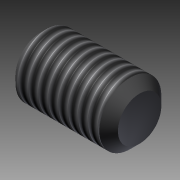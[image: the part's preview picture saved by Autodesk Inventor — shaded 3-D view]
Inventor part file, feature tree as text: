
AUTODESK INVENTOR PART (.ipt)
format: ipt  version: 2011 SP1 (Build 150282100, 282)  size: 117,248 bytes
history: native  units: mm
features: other x7, sketch x3, revolve x2, thread x1, extrude x1
ambient origin geometry x8: Origin, YZ Plane, XZ Plane, XY Plane, X Axis, Y Axis, Z Axis, Center Point
bodies: Solid1 (feature_tree)
feature tree (14):
  revolve  "Revolution1"  [1 undecoded]
  thread  "Thread1"  [1 undecoded]
  extrude  "Extrusion1"  TaperAngle=0.0deg  [1 undecoded]
  revolve  "Revolution2"  [1 undecoded]
  other  "CP_XY"
  other  "CP_YZ"
  other  "CP_ZX"
  other  "CP_X"
  other  "CP_Y"
  other  "CP_Z"
  other  "CP_Center"
  sketch  "Sketch_1"  dims[d0=360.0deg d1=6.7595mm d2=0.0mm d3=2.0mm d4=0.0mm]
  sketch  "Sketch_2"  dims[d5=360.0deg d6=0.0mm]
  sketch  "Sketch_3"
note: 4 required parameter values undecoded (feature->parameter linkage not recoverable at this tier; creation-order binding heuristic only, values carry confidence <= 0.55)